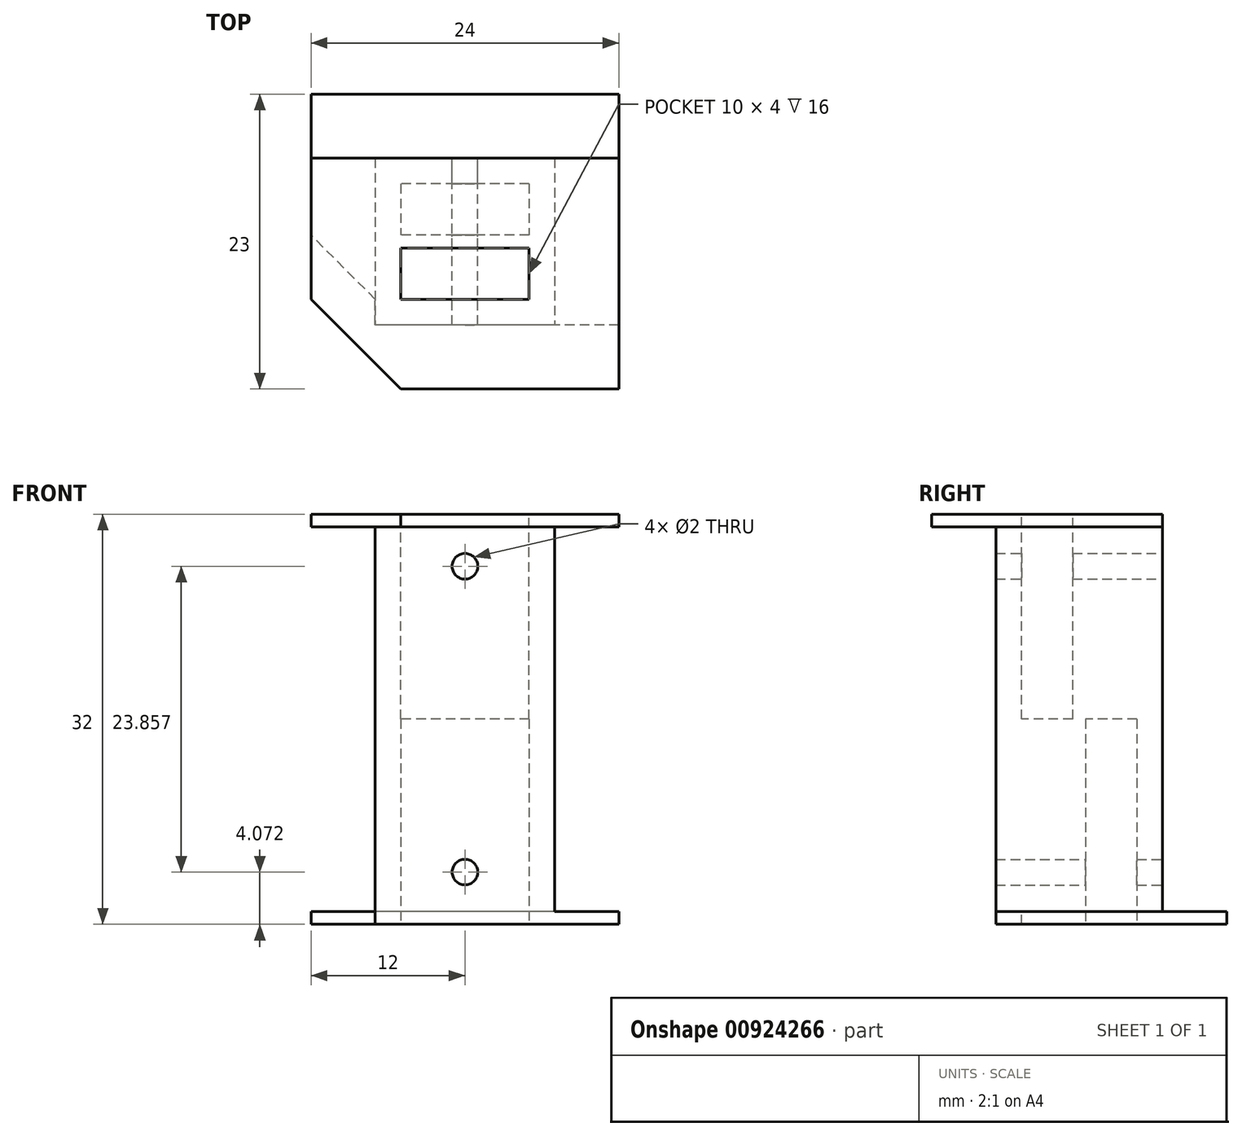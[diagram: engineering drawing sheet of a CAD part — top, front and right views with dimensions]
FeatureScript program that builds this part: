
annotation { "Feature Type Name" : "Feature", "Feature Type Description" : "" }
export const myFeature = defineFeature(function(context is Context, id is Id, definition is map)
    precondition{}
    {
        {
            var Q0;
            Q0=qCreatedBy(makeId("Top.planeOp"),FACE);
            var sketch = newSketch(context, id + "F0", { "sketchPlane" : qUnion([Q0])});
            skLineSegment(sketch, "E0.bottom", {"start": v(5, 2) * mm, "end": v(-5, 2) * mm});
            skLineSegment(sketch, "E0.top", {"start": v(5, -2) * mm, "end": v(-5, -2) * mm});
            skLineSegment(sketch, "E0.left", {"start": v(5, 2) * mm, "end": v(5, -2) * mm});
            skLineSegment(sketch, "E0.right", {"start": v(-5, 2) * mm, "end": v(-5, -2) * mm});
            skPoint(sketch, "E0.middle", {"position": v(0, 0) * mm});
            skLineSegment(sketch, "E1.0", {"start": v(7, 4) * mm, "end": v(7, -4) * mm});
            skLineSegment(sketch, "E1.1", {"start": v(7, 4) * mm, "end": v(-7, 4) * mm});
            skLineSegment(sketch, "E1.2", {"start": v(-7, 4) * mm, "end": v(-7, -4) * mm});
            skLineSegment(sketch, "E1.3", {"start": v(7, -4) * mm, "end": v(-7, -4) * mm});
            skSolve(sketch);
        }
        {
            var Q0;
            Q0=makeQuery(id+"F0.imprint","IMPRINT",FACE,{"disambiguationData":[TD([[makeQuery(id+"F0.imprint","IMPRINT",EDGE,{"derivedFrom":sQuery(id+"F0.wireOp",EDGE,"E0.bottom")}),-1.0]])]});
            extrude(context, id + "F1", {"entities" : qUnion([Q0]), "oppositeDirection" : true, "depth" : 16 * mm, "offsetDistance" : 25 * mm});
        }
        {
            var Q0;
            Q0=makeQuery(id+"F1.opExtrude","CAP_FACE",FACE,{"disambiguationData":[OSD([sQuery(id+"F0.wireOp",EDGE,"E0.bottom"),sQuery(id+"F0.wireOp",EDGE,"E0.top"),sQuery(id+"F0.wireOp",EDGE,"E0.left"),sQuery(id+"F0.wireOp",EDGE,"E0.right"),sQuery(id+"F0.wireOp",EDGE,"E1.0"),sQuery(id+"F0.wireOp",EDGE,"E1.1"),sQuery(id+"F0.wireOp",EDGE,"E1.2"),sQuery(id+"F0.wireOp",EDGE,"E1.3")])],"isStart":true});
            var sketch = newSketch(context, id + "F2", { "sketchPlane" : qUnion([Q0])});
            skLineSegment(sketch, "E2.0", {"start": v(12, 9) * mm, "end": v(-12, 9) * mm});
            skLineSegment(sketch, "E2.1", {"start": v(12, 9) * mm, "end": v(12, -9) * mm});
            skLineSegment(sketch, "E2.2", {"start": v(12, -9) * mm, "end": v(-12, -9) * mm});
            skLineSegment(sketch, "E2.3", {"start": v(-12, 9) * mm, "end": v(-12, -9) * mm});
            skSolve(sketch);
        }
        {
            var Q0;
            Q0=makeQuery(id+"F2.imprint","IMPRINT",FACE,{"disambiguationData":[TD([[makeQuery(id+"F2.imprint","IMPRINT",EDGE,{"derivedFrom":sQuery(id+"F2.wireOp",EDGE,"E2.0")}),1.0]])]});
            extrude(context, id + "F3", {"entities" : qUnion([Q0]), "oppositeDirection" : true, "depth" : 1 * mm, "offsetDistance" : 25 * mm});
        }
        {
            var Q0;
            Q0=makeQuery(id+"F3.opExtrude","SWEPT_FACE",FACE,{"disambiguationData":[OSD([sQuery(id+"F2.wireOp",EDGE,"E2.0")])]});
            var sketch = newSketch(context, id + "F4", { "sketchPlane" : qUnion([Q0])});
            skLineSegment(sketch, "E3.0", {"start": v(39.03, -4) * mm, "end": v(63.03, -4) * mm, "construction": true});
            skLineSegment(sketch, "E4.0", {"start": v(-12, -28) * mm, "end": v(12, -28) * mm});
            skCircle(sketch, "E5", {"center": v(0, -4.07) * mm, "radius": 1 * mm});
            skCircle(sketch, "E6", {"center": v(0, -28) * mm, "radius": 1 * mm});
            skSolve(sketch);
        }
        {
            var Q0;
            Q0 = qSketchRegion(id + "F4", true);
            extrude(context, id + "F5", {"entities" : qUnion([Q0]), "operationType" : NewBodyOperationType.REMOVE, "endBound" : BoundingType.THROUGH_ALL, "oppositeDirection" : true, "depth" : 25 * mm, "offsetDistance" : 25 * mm});
        }
        {
            var Q0;
            Q0=makeQuery(id+"F3.opExtrude","SWEPT_EDGE",EDGE,{"disambiguationData":[OSD([sQuery(id+"F2.wireOp",EDGE,"E2.2"),sQuery(id+"F2.wireOp",EDGE,"E2.3")])]});
            var Q1;
            Q1=makeQuery(id+"FPhxryXbHbcSL3D_2.opPattern","COPY",EDGE,{"derivedFrom":makeQuery(id+"F3.opExtrude","SWEPT_EDGE",EDGE,{"disambiguationData":[OSD([sQuery(id+"F2.wireOp",EDGE,"E2.2"),sQuery(id+"F2.wireOp",EDGE,"E2.3")])]}),"instanceName":"1"});
            chamfer(context, id + "F6", {"entities" : qUnion([Q0, Q1]), "width" : 7 * mm, "tangentPropagation" : true});
        }
        {
            var Q0;
            Q0=makeQuery(id+"F3.opExtrude","SWEPT_BODY",BODY,{"disambiguationData":[OSD([sQuery(id+"F0.wireOp",EDGE,"E1.0"),sQuery(id+"F0.wireOp",EDGE,"E1.1"),sQuery(id+"F0.wireOp",EDGE,"E1.2"),sQuery(id+"F0.wireOp",EDGE,"E1.3"),sQuery(id+"F2.wireOp",EDGE,"E2.0"),sQuery(id+"F2.wireOp",EDGE,"E2.1"),sQuery(id+"F2.wireOp",EDGE,"E2.2"),sQuery(id+"F2.wireOp",EDGE,"E2.3")])]});
            var Q1;
            Q1=makeQuery(id+"F1.opExtrude","SWEPT_BODY",BODY,{"disambiguationData":[OSD([sQuery(id+"F0.wireOp",EDGE,"E0.bottom"),sQuery(id+"F0.wireOp",EDGE,"E0.top"),sQuery(id+"F0.wireOp",EDGE,"E0.left"),sQuery(id+"F0.wireOp",EDGE,"E0.right"),sQuery(id+"F0.wireOp",EDGE,"E1.0"),sQuery(id+"F0.wireOp",EDGE,"E1.1"),sQuery(id+"F0.wireOp",EDGE,"E1.2"),sQuery(id+"F0.wireOp",EDGE,"E1.3")])]});
            var Q2;
            Q2=makeQuery(id+"F1.opExtrude","CAP_FACE",FACE,{"disambiguationData":[OSD([sQuery(id+"F0.wireOp",EDGE,"E0.bottom"),sQuery(id+"F0.wireOp",EDGE,"E0.top"),sQuery(id+"F0.wireOp",EDGE,"E0.left"),sQuery(id+"F0.wireOp",EDGE,"E0.right"),sQuery(id+"F0.wireOp",EDGE,"E1.0"),sQuery(id+"F0.wireOp",EDGE,"E1.1"),sQuery(id+"F0.wireOp",EDGE,"E1.2"),sQuery(id+"F0.wireOp",EDGE,"E1.3")])],"isStart":false});
            mirror(context, id + "F7", {"entities" : qUnion([Q0, Q1]), "mirrorPlane" : qUnion([Q2])});
        }
        {
            var Q0;
            Q0=makeQuery(id+"F7.opPattern","COPY",BODY,{"derivedFrom":makeQuery(id+"F1.opExtrude","SWEPT_BODY",BODY,{"disambiguationData":[OSD([sQuery(id+"F0.wireOp",EDGE,"E0.bottom"),sQuery(id+"F0.wireOp",EDGE,"E0.top"),sQuery(id+"F0.wireOp",EDGE,"E0.left"),sQuery(id+"F0.wireOp",EDGE,"E0.right"),sQuery(id+"F0.wireOp",EDGE,"E1.0"),sQuery(id+"F0.wireOp",EDGE,"E1.1"),sQuery(id+"F0.wireOp",EDGE,"E1.2"),sQuery(id+"F0.wireOp",EDGE,"E1.3")])]}),"instanceName":"1"});
            var Q1;
            Q1=makeQuery(id+"F7.opPattern","COPY",BODY,{"derivedFrom":makeQuery(id+"F3.opExtrude","SWEPT_BODY",BODY,{"disambiguationData":[OSD([sQuery(id+"F0.wireOp",EDGE,"E1.0"),sQuery(id+"F0.wireOp",EDGE,"E1.1"),sQuery(id+"F0.wireOp",EDGE,"E1.2"),sQuery(id+"F0.wireOp",EDGE,"E1.3"),sQuery(id+"F2.wireOp",EDGE,"E2.0"),sQuery(id+"F2.wireOp",EDGE,"E2.1"),sQuery(id+"F2.wireOp",EDGE,"E2.2"),sQuery(id+"F2.wireOp",EDGE,"E2.3")])]}),"instanceName":"1"});
            var Q2;
            Q2=makeQuery(id+"F7.opPattern","COPY",EDGE,{"derivedFrom":makeQuery(id+"F1.opExtrude","SWEPT_EDGE",EDGE,{"disambiguationData":[OSD([sQuery(id+"F0.wireOp",EDGE,"E1.1"),sQuery(id+"F0.wireOp",EDGE,"E1.2")])]}),"instanceName":"1"});
            transform(context, id + "F8", {"entities" : qUnion([Q0, Q1]), "transformType" : TransformType.TRANSLATION_3D, "dx" : 0 * mm, "dy" : 5 * mm, "dz" : 0 * mm, "makeCopy" : false});
        }
        {
            var Q0;
            Q0=makeQuery(id+"F7.opPattern","COPY",FACE,{"derivedFrom":makeQuery(id+"F1.opExtrude","SWEPT_FACE",FACE,{"disambiguationData":[OSD([sQuery(id+"F0.wireOp",EDGE,"E1.3")])]}),"instanceName":"1"});
            var Q1;
            Q1=makeQuery(id+"F1.opExtrude","SWEPT_FACE",FACE,{"disambiguationData":[OSD([sQuery(id+"F0.wireOp",EDGE,"E1.3")])]});
            extrude(context, id + "F9", {"entities" : qUnion([Q0]), "operationType" : NewBodyOperationType.ADD, "endBound" : BoundingType.UP_TO_SURFACE, "depth" : 25 * mm, "endBoundEntityFace" : qUnion([Q1]), "offsetDistance" : 25 * mm});
        }
        {
            var Q0;
            Q0=makeQuery(id+"F1.opExtrude","SWEPT_FACE",FACE,{"disambiguationData":[OSD([sQuery(id+"F0.wireOp",EDGE,"E1.1")])]});
            var Q1;
            Q1=makeQuery(id+"F7.opPattern","COPY",FACE,{"derivedFrom":makeQuery(id+"F1.opExtrude","SWEPT_FACE",FACE,{"disambiguationData":[OSD([sQuery(id+"F0.wireOp",EDGE,"E1.1")])]}),"instanceName":"1"});
            extrude(context, id + "F10", {"entities" : qUnion([Q0]), "operationType" : NewBodyOperationType.ADD, "endBound" : BoundingType.UP_TO_SURFACE, "depth" : 25 * mm, "endBoundEntityFace" : qUnion([Q1]), "offsetDistance" : 25 * mm});
        }
    });
